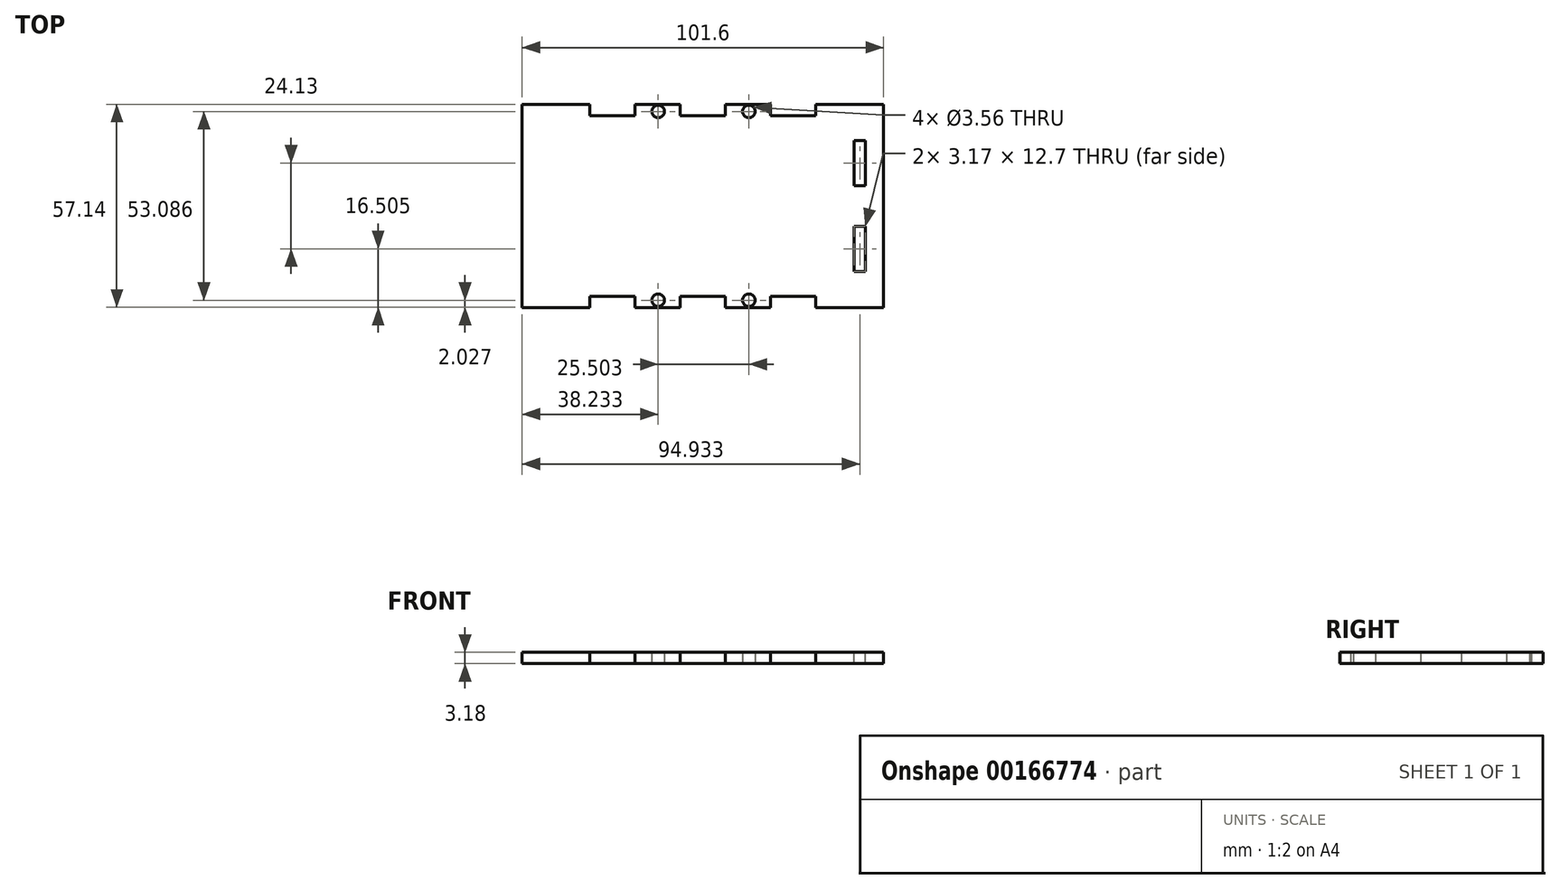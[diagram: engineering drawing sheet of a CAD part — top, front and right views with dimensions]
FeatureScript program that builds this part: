
annotation { "Feature Type Name" : "Feature", "Feature Type Description" : "" }
export const myFeature = defineFeature(function(context is Context, id is Id, definition is map)
    precondition{}
    {
        {
            var Q0;
            Q0=qCreatedBy(makeId("Top.planeOp"),FACE);
            var sketch = newSketch(context, id + "F0", { "sketchPlane" : qUnion([Q0])});
            skLineSegment(sketch, "E0.bottom", {"start": v(50.8, -28.58) * mm, "end": v(-50.8, -28.58) * mm});
            skLineSegment(sketch, "E0.top", {"start": v(50.8, 28.58) * mm, "end": v(-50.8, 28.57) * mm});
            skLineSegment(sketch, "E0.left", {"start": v(50.8, -28.58) * mm, "end": v(50.8, 28.58) * mm});
            skLineSegment(sketch, "E0.right", {"start": v(-50.8, -28.58) * mm, "end": v(-50.8, 28.57) * mm});
            skPoint(sketch, "E0.middle", {"position": v(0, 0) * mm});
            skSolve(sketch);
        }
        {
            var Q0;
            Q0 = qSketchRegion(id + "F0", true);
            extrude(context, id + "F1", {"entities" : qUnion([Q0]), "depth" : 3.17 * mm});
        }
        {
            var Q0;
            Q0=makeQuery(id+"F1.opExtrude","CAP_FACE",FACE,{"disambiguationData":[OSD([sQuery(id+"F0.wireOp",EDGE,"E0.bottom"),sQuery(id+"F0.wireOp",EDGE,"E0.top"),sQuery(id+"F0.wireOp",EDGE,"E0.left"),sQuery(id+"F0.wireOp",EDGE,"E0.right")])],"isStart":false});
            var sketch = newSketch(context, id + "F2", { "sketchPlane" : qUnion([Q0])});
            skLineSegment(sketch, "E1.bottom", {"start": v(42.55, -5.72) * mm, "end": v(45.72, -5.72) * mm});
            skLineSegment(sketch, "E1.top", {"start": v(42.55, -18.42) * mm, "end": v(45.72, -18.42) * mm});
            skLineSegment(sketch, "E1.left", {"start": v(42.55, -5.72) * mm, "end": v(42.55, -18.42) * mm});
            skLineSegment(sketch, "E1.right", {"start": v(45.72, -5.72) * mm, "end": v(45.72, -18.42) * mm});
            skLineSegment(sketch, "E2.MirrorCS", {"start": v(42.55, 5.72) * mm, "end": v(45.72, 5.72) * mm});
            skLineSegment(sketch, "E3.MirrorCS", {"start": v(42.55, 18.42) * mm, "end": v(45.72, 18.42) * mm});
            skLineSegment(sketch, "E4.MirrorCS", {"start": v(42.55, 5.72) * mm, "end": v(42.54, 18.42) * mm});
            skLineSegment(sketch, "E5.MirrorCS", {"start": v(45.72, 5.72) * mm, "end": v(45.72, 18.42) * mm});
            skLineSegment(sketch, "E6", {"start": v(31.75, -25.4) * mm, "end": v(19.05, -25.4) * mm});
            skLineSegment(sketch, "E7", {"start": v(19.05, -25.4) * mm, "end": v(19.05, -28.58) * mm});
            skLineSegment(sketch, "E8", {"start": v(31.75, -28.58) * mm, "end": v(31.75, -25.4) * mm});
            skLineSegment(sketch, "E9", {"start": v(6.35, -28.58) * mm, "end": v(6.35, -25.4) * mm});
            skLineSegment(sketch, "E10", {"start": v(6.35, -25.4) * mm, "end": v(-6.35, -25.4) * mm});
            skLineSegment(sketch, "E11", {"start": v(-6.35, -25.4) * mm, "end": v(-6.35, -28.58) * mm});
            skLineSegment(sketch, "E12", {"start": v(-19.05, -28.58) * mm, "end": v(-19.05, -25.4) * mm});
            skLineSegment(sketch, "E13", {"start": v(-19.05, -25.4) * mm, "end": v(-31.75, -25.4) * mm});
            skLineSegment(sketch, "E14", {"start": v(-31.75, -25.4) * mm, "end": v(-31.75, -28.58) * mm});
            skLineSegment(sketch, "E15", {"start": v(-31.75, -28.58) * mm, "end": v(-19.05, -28.58) * mm});
            skLineSegment(sketch, "E16", {"start": v(-6.35, -28.58) * mm, "end": v(6.35, -28.58) * mm});
            skLineSegment(sketch, "E17", {"start": v(19.05, -28.58) * mm, "end": v(31.75, -28.58) * mm});
            skLineSegment(sketch, "E18.MirrorCS", {"start": v(-31.75, 25.4) * mm, "end": v(-31.75, 28.58) * mm});
            skLineSegment(sketch, "E19.MirrorCS", {"start": v(-19.05, 25.4) * mm, "end": v(-31.75, 25.4) * mm});
            skLineSegment(sketch, "E20.MirrorCS", {"start": v(-19.05, 28.58) * mm, "end": v(-19.05, 25.4) * mm});
            skLineSegment(sketch, "E21.MirrorCS", {"start": v(-31.75, 28.58) * mm, "end": v(-19.05, 28.58) * mm});
            skLineSegment(sketch, "E22.MirrorCS", {"start": v(-6.35, 28.58) * mm, "end": v(6.35, 28.58) * mm});
            skLineSegment(sketch, "E23.MirrorCS", {"start": v(6.35, 25.4) * mm, "end": v(-6.35, 25.4) * mm});
            skLineSegment(sketch, "E24.MirrorCS", {"start": v(-6.35, 25.4) * mm, "end": v(-6.35, 28.58) * mm});
            skLineSegment(sketch, "E25.MirrorCS", {"start": v(6.35, 28.58) * mm, "end": v(6.35, 25.4) * mm});
            skLineSegment(sketch, "E26.MirrorCS", {"start": v(19.05, 28.58) * mm, "end": v(31.75, 28.58) * mm});
            skLineSegment(sketch, "E27.MirrorCS", {"start": v(31.75, 25.4) * mm, "end": v(19.05, 25.4) * mm});
            skLineSegment(sketch, "E28.MirrorCS", {"start": v(19.05, 25.4) * mm, "end": v(19.05, 28.58) * mm});
            skLineSegment(sketch, "E29.MirrorCS", {"start": v(31.75, 28.58) * mm, "end": v(31.75, 25.4) * mm});
            skSolve(sketch);
        }
        {
            var Q0;
            Q0=makeQuery(id+"F2.imprint","IMPRINT",FACE,{"disambiguationData":[TD([[makeQuery(id+"F2.imprint","IMPRINT",EDGE,{"derivedFrom":sQuery(id+"F2.wireOp",EDGE,"E12")}),1.0]])]});
            var Q1;
            Q1=makeQuery(id+"F2.imprint","IMPRINT",FACE,{"disambiguationData":[TD([[makeQuery(id+"F2.imprint","IMPRINT",EDGE,{"derivedFrom":sQuery(id+"F2.wireOp",EDGE,"E9")}),1.0]])]});
            var Q2;
            Q2=makeQuery(id+"F2.imprint","IMPRINT",FACE,{"disambiguationData":[TD([[makeQuery(id+"F2.imprint","IMPRINT",EDGE,{"derivedFrom":sQuery(id+"F2.wireOp",EDGE,"E6")}),1.0]])]});
            var Q3;
            Q3=makeQuery(id+"F2.imprint","IMPRINT",FACE,{"disambiguationData":[TD([[makeQuery(id+"F2.imprint","IMPRINT",EDGE,{"derivedFrom":sQuery(id+"F2.wireOp",EDGE,"E1.bottom")}),-1.0]])]});
            var Q4;
            Q4=makeQuery(id+"F2.imprint","IMPRINT",FACE,{"disambiguationData":[TD([[makeQuery(id+"F2.imprint","IMPRINT",EDGE,{"derivedFrom":sQuery(id+"F2.wireOp",EDGE,"E2.MirrorCS")}),1.0]])]});
            var Q5;
            Q5=makeQuery(id+"F2.imprint","IMPRINT",FACE,{"disambiguationData":[TD([[makeQuery(id+"F2.imprint","IMPRINT",EDGE,{"derivedFrom":sQuery(id+"F2.wireOp",EDGE,"E18.MirrorCS")}),-1.0]])]});
            var Q6;
            Q6=makeQuery(id+"F2.imprint","IMPRINT",FACE,{"disambiguationData":[TD([[makeQuery(id+"F2.imprint","IMPRINT",EDGE,{"derivedFrom":sQuery(id+"F2.wireOp",EDGE,"E22.MirrorCS")}),1.0]])]});
            var Q7;
            Q7=makeQuery(id+"F2.imprint","IMPRINT",FACE,{"disambiguationData":[TD([[makeQuery(id+"F2.imprint","IMPRINT",EDGE,{"derivedFrom":sQuery(id+"F2.wireOp",EDGE,"E26.MirrorCS")}),1.0]])]});
            extrude(context, id + "F3", {"entities" : qUnion([Q0, Q1, Q2, Q3, Q4, Q5, Q6, Q7]), "operationType" : NewBodyOperationType.REMOVE, "endBound" : BoundingType.THROUGH_ALL, "oppositeDirection" : true, "depth" : 25.4 * mm});
        }
        {
            var Q0;
            Q0=makeQuery(id+"F1.opExtrude","CAP_FACE",FACE,{"disambiguationData":[OSD([sQuery(id+"F0.wireOp",EDGE,"E0.bottom"),sQuery(id+"F0.wireOp",EDGE,"E0.top"),sQuery(id+"F0.wireOp",EDGE,"E0.left"),sQuery(id+"F0.wireOp",EDGE,"E0.right")])],"isStart":true});
            var sketch = newSketch(context, id + "F4", { "sketchPlane" : qUnion([Q0])});
            skCircle(sketch, "E30", {"center": v(-12.57, 26.54) * mm, "radius": 2.03 * mm});
            skCircle(sketch, "E31", {"center": v(12.94, 26.54) * mm, "radius": 2.03 * mm});
            skCircle(sketch, "E32.MirrorC", {"center": v(12.94, -26.54) * mm, "radius": 2.03 * mm});
            skCircle(sketch, "E33.MirrorC", {"center": v(-12.57, -26.54) * mm, "radius": 2.03 * mm});
            skSolve(sketch);
        }
        {
            var Q0;
            Q0=sQuery(id+"F4.wireOp",VERTEX,"E30.center");
            var Q1;
            Q1=sQuery(id+"F4.wireOp",VERTEX,"E31.center");
            var Q2;
            Q2=sQuery(id+"F4.wireOp",VERTEX,"E33.MirrorC.center");
            var Q3;
            Q3=sQuery(id+"F4.wireOp",VERTEX,"E32.MirrorC.center");
            var Q4;
            Q4=makeQuery(id+"F1.opExtrude","SWEPT_BODY",BODY,{"disambiguationData":[OSD([sQuery(id+"F0.wireOp",EDGE,"E0.bottom"),sQuery(id+"F0.wireOp",EDGE,"E0.top"),sQuery(id+"F0.wireOp",EDGE,"E0.left"),sQuery(id+"F0.wireOp",EDGE,"E0.right")])]});
            hole(context, id + "F5", {"style" : HoleStyle.SIMPLE, "endStyle" : HoleEndStyle.THROUGH, "holeDiameter" : 3.56 * mm, "locations" : qUnion([Q0, Q1, Q2, Q3]), "scope" : qUnion([Q4]), "isTappedThrough" : true});
        }
    });
